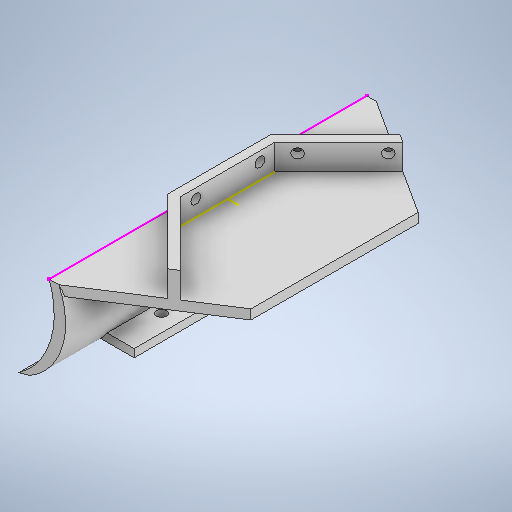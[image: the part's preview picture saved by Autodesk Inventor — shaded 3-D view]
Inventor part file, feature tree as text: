
AUTODESK INVENTOR PART (.ipt)
format: ipt  version: 2025.1 (Build 291241020, 241B)  size: 318,464 bytes
history: native  units: in
note: dims shown in document units (in); Inventor stores cm internally (conversion verified against a paired STEP export)
features: other x3, sketch x3, extrude x2
ambient origin geometry x8: Origin, YZ Plane, XZ Plane, XY Plane, X Axis, Y Axis, Z Axis, Center Point
bodies: Solid1 (feature_tree)
feature tree (8):
  other  "slopeAssembly.iam"
  other  "slope.ipt:1"
  other  "distanceSensorMountIncl.ipt:1"
  extrude  "Extrusion1"  Depth=0.3937in TaperAngle=0.0deg
  extrude  "Extrusion2"  Depth=0.3937in TaperAngle=0.0deg
  sketch  "Sketch12_1"  dims[d0=0.3937in d1=1.0in d2=0.0in]
  sketch  "Sketch3"  dims[d3=0.3937in d4=1.0in d5=0.0in]
  sketch  "Sketch4"
